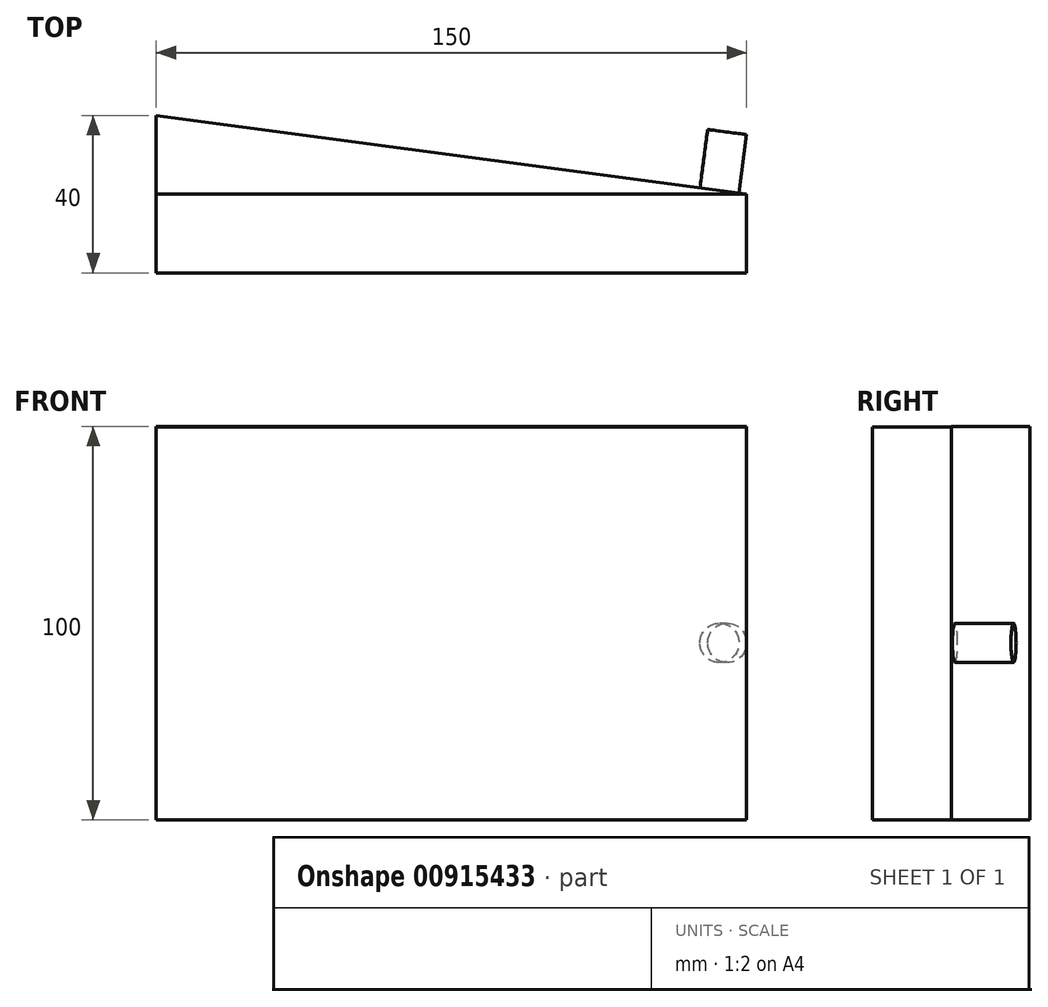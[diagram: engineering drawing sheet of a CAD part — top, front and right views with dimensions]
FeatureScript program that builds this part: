
annotation { "Feature Type Name" : "Feature", "Feature Type Description" : "" }
export const myFeature = defineFeature(function(context is Context, id is Id, definition is map)
    precondition{}
    {
        {
            var Q0;
            Q0=qCreatedBy(makeId("Top.planeOp"),FACE);
            var sketch = newSketch(context, id + "F0", { "sketchPlane" : qUnion([Q0])});
            skLineSegment(sketch, "E0.top", {"start": v(75, -10) * mm, "end": v(-75, -10) * mm});
            skLineSegment(sketch, "E0.right", {"start": v(-75, 10) * mm, "end": v(-75, -10) * mm});
            skPoint(sketch, "E0.middle", {"position": v(0, 0) * mm});
            skLineSegment(sketch, "E1", {"start": v(-75, 10) * mm, "end": v(75, -10) * mm});
            skSolve(sketch);
        }
        {
            var Q0;
            Q0=makeQuery(id+"F0.imprint","IMPRINT",FACE,{"disambiguationData":[TD([[makeQuery(id+"F0.imprint","IMPRINT",EDGE,{"derivedFrom":sQuery(id+"F0.wireOp",EDGE,"E0.top")}),-1.0]])]});
            extrude(context, id + "F1", {"entities" : qUnion([Q0]), "depth" : 100 * mm, "offsetDistance" : 25 * mm});
        }
        {
            var Q0;
            Q0=makeQuery(id+"F1.opExtrude","SWEPT_FACE",FACE,{"disambiguationData":[OSD([sQuery(id+"F0.wireOp",EDGE,"E0.top")])]});
            var sketch = newSketch(context, id + "F2", { "sketchPlane" : qUnion([Q0])});
            skLineSegment(sketch, "E2.bottom", {"start": v(75, 99.87) * mm, "end": v(-75, 99.87) * mm});
            skLineSegment(sketch, "E2.top", {"start": v(75, -0.13) * mm, "end": v(-75, -0.13) * mm});
            skLineSegment(sketch, "E2.left", {"start": v(75, 99.87) * mm, "end": v(75, -0.13) * mm});
            skLineSegment(sketch, "E2.right", {"start": v(-75, 99.87) * mm, "end": v(-75, -0.13) * mm});
            skPoint(sketch, "E2.middle", {"position": v(0, 49.87) * mm});
            skSolve(sketch);
        }
        {
            var Q0;
            {var subQ0=sQuery(id+"F2.wireOp",EDGE,"E2.bottom");Q0=makeQuery(id+"F2.imprint","IMPRINT",FACE,{"disambiguationData":[TD([[makeQuery(id+"F2.imprint","IMPRINT",EDGE,{"derivedFrom":subQ0}),1.0]])]});}
            extrude(context, id + "F3", {"entities" : qUnion([Q0]), "operationType" : NewBodyOperationType.ADD, "depth" : 20 * mm, "offsetDistance" : 25 * mm});
        }
        {
            var Q0;
            Q0=makeQuery(id+"F1.opExtrude","SWEPT_FACE",FACE,{"disambiguationData":[OSD([sQuery(id+"F0.wireOp",EDGE,"E1")])]});
            var sketch = newSketch(context, id + "F4", { "sketchPlane" : qUnion([Q0])});
            skCircle(sketch, "E3", {"center": v(-68.66, 45) * mm, "radius": 5 * mm});
            skSolve(sketch);
        }
        {
            var Q0;
            Q0=makeQuery(id+"F4.imprint","IMPRINT",FACE,{"disambiguationData":[TD([[makeQuery(id+"F4.imprint","IMPRINT",EDGE,{"derivedFrom":sQuery(id+"F4.wireOp",EDGE,"E3")}),1.0]])]});
            extrude(context, id + "F5", {"entities" : qUnion([Q0]), "operationType" : NewBodyOperationType.ADD, "depth" : 15 * mm, "offsetDistance" : 25 * mm});
        }
    });
